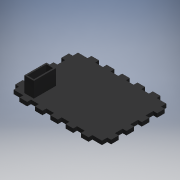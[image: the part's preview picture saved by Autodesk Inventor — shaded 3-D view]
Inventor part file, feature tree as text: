
AUTODESK INVENTOR PART (.ipt)
format: ipt  version: 2019 (Build 230136000, 136)  size: 233,472 bytes
history: native  units: mm
features: extrude x4, sketch x3
ambient origin geometry x8: Origin, YZ Plane, XZ Plane, XY Plane, X Axis, Y Axis, Z Axis, Center Point
bodies: Solid1 (feature_tree)
feature tree (7):
  extrude  "Extrusion1"  Depth=75.0mm
  extrude  "Extrusion3"  Depth=8.0mm
  extrude  "Extrusion4"  Depth=8.0mm
  extrude  "Extrusion5"  Depth=8.0mm
  sketch  "Sketch1"  dims[d0=100.0mm d1=75.0mm]
  sketch  "Sketch4"  dims[d2=4.0mm d3=0.0mm d9=8.0mm]
  sketch  "Sketch5"  dims[d11=4.0mm d12=8.0mm d13=8.0mm d14=8.0mm d15=8.0mm d16=8.0mm d17=4.0mm d18=8.0mm d19=4.0mm d20=0.0mm d22=4.0mm d23=7.0mm d24=20.0mm d26=8.0mm d27=10.0mm d28=0.0mm d29=1.5mm d30=16.0mm d31=0.0mm d32=14.0mm]
